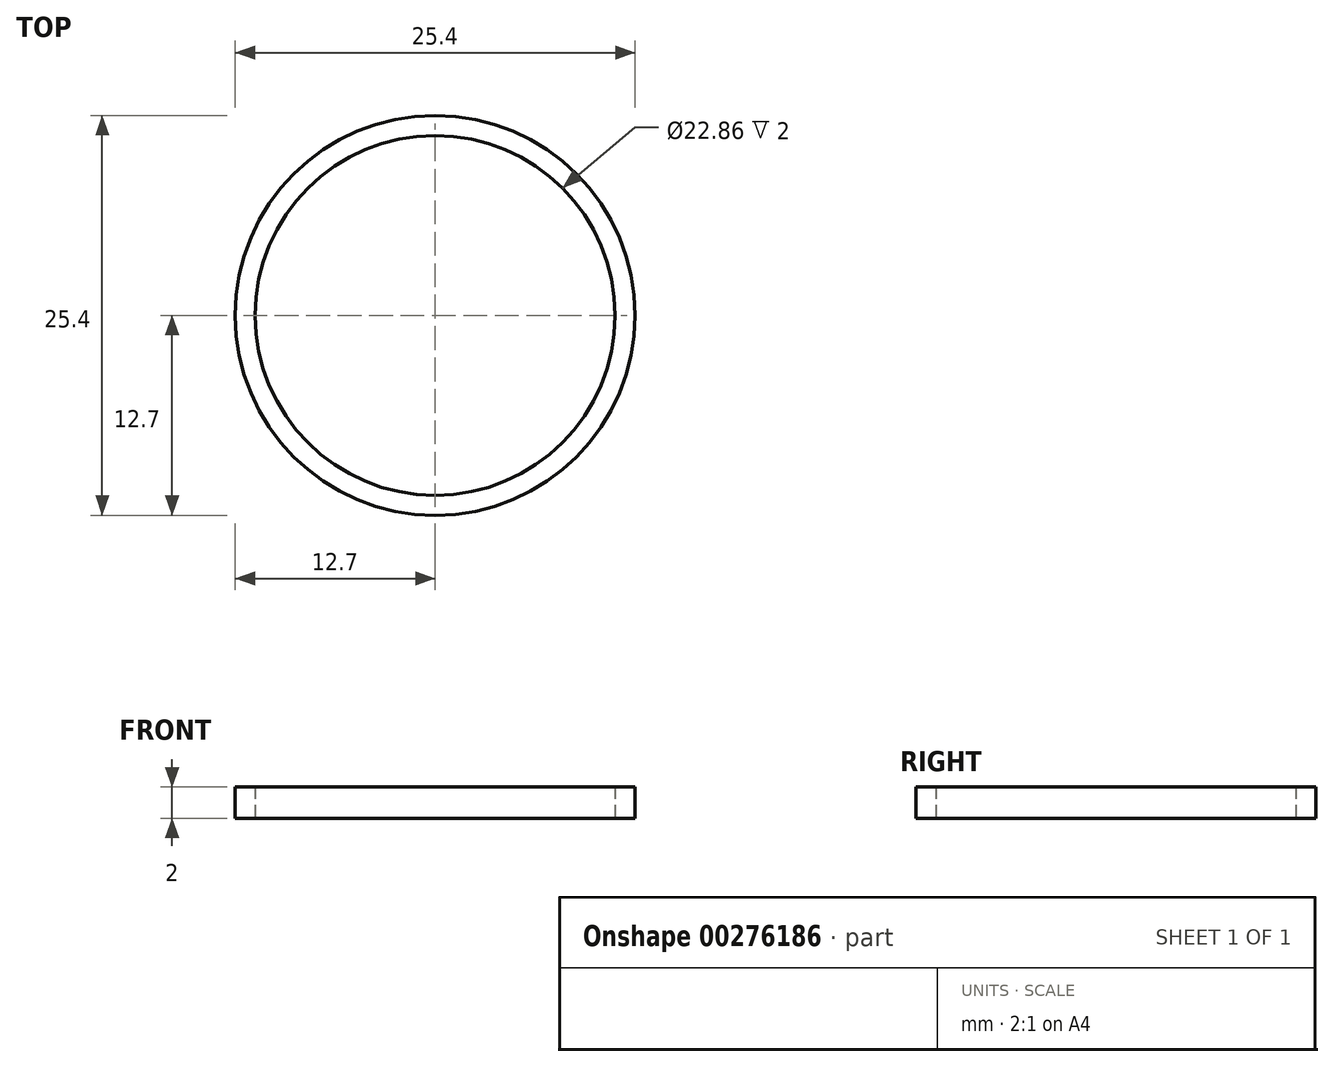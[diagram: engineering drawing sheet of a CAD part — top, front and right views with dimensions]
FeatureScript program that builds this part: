
annotation { "Feature Type Name" : "Feature", "Feature Type Description" : "" }
export const myFeature = defineFeature(function(context is Context, id is Id, definition is map)
    precondition{}
    {
        {
            var Q0;
            Q0=qCreatedBy(makeId("Top.planeOp"),FACE);
            var sketch = newSketch(context, id + "F0", { "sketchPlane" : qUnion([Q0])});
            skCircle(sketch, "E0", {"center": v(0, 0) * mm, "radius": 12.7 * mm});
            skCircle(sketch, "E1", {"center": v(0, 0) * mm, "radius": 11.43 * mm});
            skSolve(sketch);
        }
        {
            var Q0;
            Q0 = qSketchRegion(id + "F0", true);
            extrude(context, id + "F1", {"entities" : qUnion([Q0]), "depth" : 2 * mm});
        }
    });
